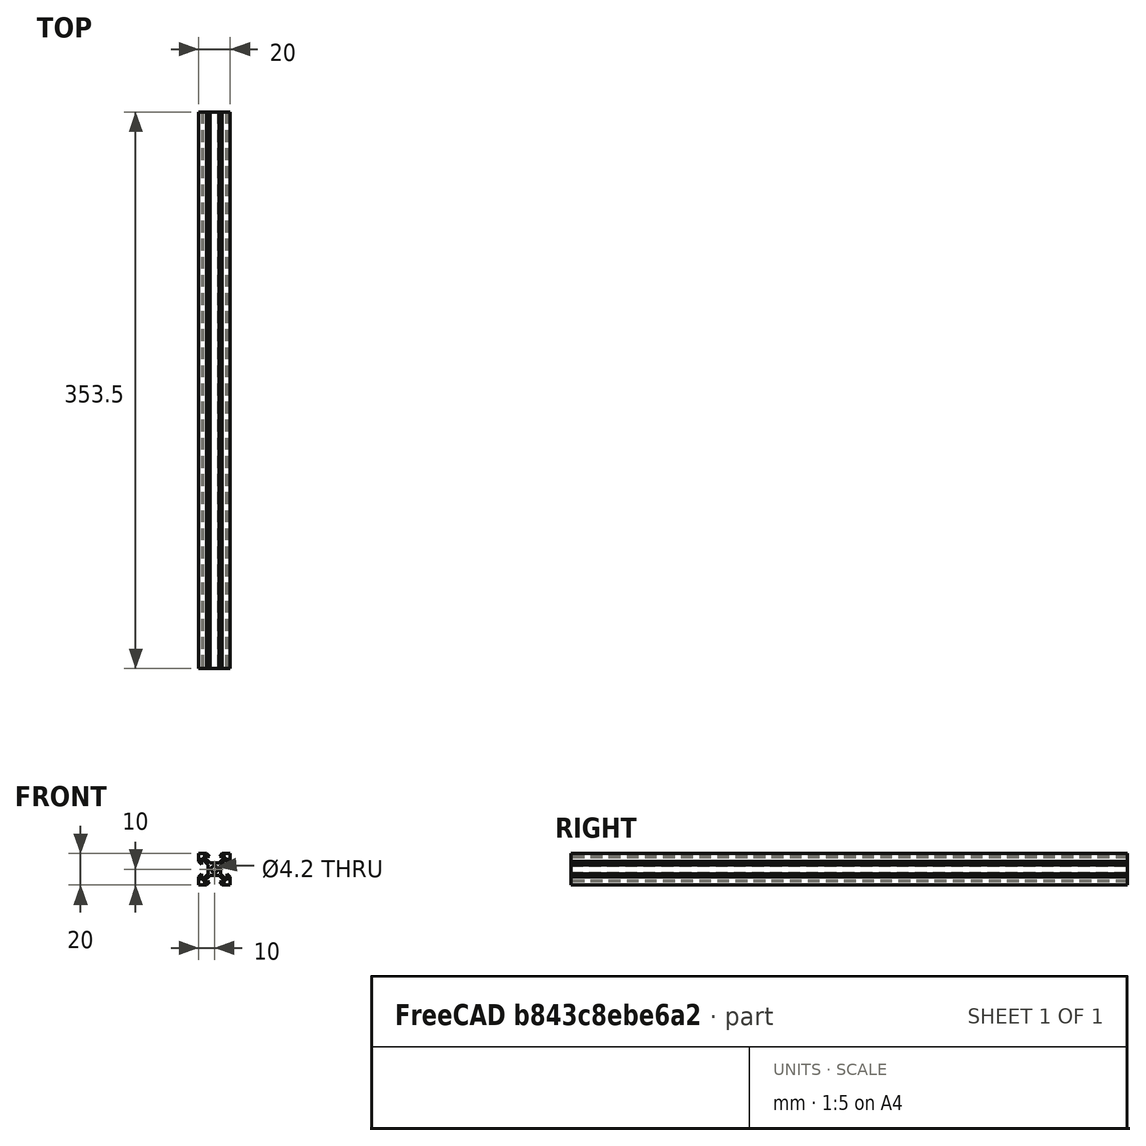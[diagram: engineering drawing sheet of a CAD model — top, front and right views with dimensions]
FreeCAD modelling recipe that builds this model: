
FCSTD DOCUMENT  (FreeCAD 0.20R29177 (Git))
Label: Vlot short Y
License: All rights reserved
LicenseURL: http://en.wikipedia.org/wiki/All_rights_reserved
objects: Sketcher::SketchObject×1, PartDesign::Pad×1, PartDesign::Body×1
note: 4 computed .brp shape members not serialized (recipe doc carries the construction recipe); baked Part::Feature solids carry a one-line shape summary decoded from their .brp

FEATURE [Sketcher::SketchObject] Sketch
  FullyConstrained = true
  MapMode = 5
  Placement = pos=(0,0,0) rot=(1,0,0;1.5708rad)
  Support = -> [XZ_Plane]
  sketch-geometry (43):
    g0: LineSegment StartX=0 StartY=0 StartZ=0 EndX=5.05 EndY=0 EndZ=0
    g1: LineSegment StartX=20 StartY=20 StartZ=0 EndX=14.95 EndY=20 EndZ=0
    g2: LineSegment StartX=0 StartY=20 StartZ=0 EndX=0 EndY=14.95 EndZ=0
    g3: LineSegment StartX=5.05 StartY=20 StartZ=0 EndX=6.9 EndY=18.15 EndZ=0
    g4: LineSegment StartX=6.9 StartY=18.15 StartZ=0 EndX=2.91066 EndY=18.15 EndZ=0
    g5: LineSegment StartX=2.91066 StartY=18.15 StartZ=0 EndX=7.16066 EndY=13.9 EndZ=0
    g6: LineSegment StartX=7.16066 StartY=13.9 StartZ=0 EndX=12.8393 EndY=13.9 EndZ=0
    g7: LineSegment StartX=12.8393 StartY=13.9 StartZ=0 EndX=17.0893 EndY=18.15 EndZ=0
    g8: LineSegment StartX=17.0893 StartY=18.15 StartZ=0 EndX=13.1 EndY=18.15 EndZ=0
    g9: LineSegment StartX=13.1 StartY=18.15 StartZ=0 EndX=14.95 EndY=20 EndZ=0
    g10: LineSegment StartX=0 StartY=20 StartZ=0 EndX=2.91066 EndY=18.15 EndZ=0
    g11: LineSegment StartX=17.0893 StartY=18.15 StartZ=0 EndX=20 EndY=20 EndZ=0
    g12: LineSegment StartX=0 StartY=20 StartZ=0 EndX=20 EndY=0 EndZ=0
    g13: LineSegment StartX=5.05 StartY=20 StartZ=0 EndX=0 EndY=20 EndZ=0
    g14: LineSegment StartX=0 StartY=20 StartZ=0 EndX=20 EndY=20 EndZ=0
    g15: LineSegment StartX=20 StartY=14.95 StartZ=0 EndX=18.15 EndY=13.1 EndZ=0
    g16: LineSegment StartX=18.15 StartY=13.1 StartZ=0 EndX=18.15 EndY=17.0893 EndZ=0
    g17: LineSegment StartX=18.15 StartY=17.0893 StartZ=0 EndX=13.9 EndY=12.8393 EndZ=0
    g18: LineSegment StartX=13.9 StartY=12.8393 StartZ=0 EndX=13.9 EndY=7.16066 EndZ=0
    g19: LineSegment StartX=13.9 StartY=7.16066 StartZ=0 EndX=18.15 EndY=2.91066 EndZ=0
    g20: LineSegment StartX=20 StartY=14.95 StartZ=0 EndX=20 EndY=20 EndZ=0
    g21: LineSegment StartX=18.15 StartY=2.91066 StartZ=0 EndX=18.15 EndY=6.9 EndZ=0
    g22: LineSegment StartX=18.15 StartY=6.9 StartZ=0 EndX=20 EndY=5.05 EndZ=0
    g23: LineSegment StartX=20 StartY=5.05 StartZ=0 EndX=20 EndY=0 EndZ=0
    g24: LineSegment StartX=5.05 StartY=0 StartZ=0 EndX=6.9 EndY=1.85 EndZ=0
    g25: LineSegment StartX=6.9 StartY=1.85 StartZ=0 EndX=2.91066 EndY=1.85 EndZ=0
    g26: LineSegment StartX=2.91066 StartY=1.85 StartZ=0 EndX=7.16066 EndY=6.1 EndZ=0
    g27: LineSegment StartX=7.16066 StartY=6.1 StartZ=0 EndX=12.8393 EndY=6.1 EndZ=0
    g28: LineSegment StartX=12.8393 StartY=6.1 StartZ=0 EndX=17.0893 EndY=1.85 EndZ=0
    g29: LineSegment StartX=17.0893 StartY=1.85 StartZ=0 EndX=13.1 EndY=1.85 EndZ=0
    g30: LineSegment StartX=13.1 StartY=1.85 StartZ=0 EndX=14.95 EndY=0 EndZ=0
    g31: LineSegment StartX=14.95 StartY=0 StartZ=0 EndX=20 EndY=0 EndZ=0
    g32: LineSegment StartX=0 StartY=14.95 StartZ=0 EndX=1.85 EndY=13.1 EndZ=0
    g33: LineSegment StartX=1.85 StartY=13.1 StartZ=0 EndX=1.85 EndY=17.0893 EndZ=0
    g34: LineSegment StartX=1.85 StartY=17.0893 StartZ=0 EndX=6.1 EndY=12.8393 EndZ=0
    g35: LineSegment StartX=6.1 StartY=12.8393 StartZ=0 EndX=6.1 EndY=7.16066 EndZ=0
    g36: LineSegment StartX=6.1 StartY=7.16066 StartZ=0 EndX=1.85 EndY=2.91066 EndZ=0
    g37: LineSegment StartX=1.85 StartY=2.91066 StartZ=0 EndX=1.85 EndY=6.9 EndZ=0
    g38: LineSegment StartX=1.85 StartY=6.9 StartZ=0 EndX=-2e-16 EndY=5.05 EndZ=0
    g39: LineSegment StartX=-2e-16 StartY=5.05 StartZ=0 EndX=0 EndY=0 EndZ=0
    g40: LineSegment StartX=0 StartY=20 StartZ=0 EndX=0 EndY=0 EndZ=0
    g41: LineSegment StartX=0 StartY=0 StartZ=0 EndX=10 EndY=10 EndZ=0
    g42: Circle CenterX=10 CenterY=10 CenterZ=0 NormalX=0 NormalY=0 NormalZ=1 AngleXU=0 Radius=2.1
  constraints (119):
    c: Coincident(g20,g1)
    c: Coincident(g13,g2)
    c: Coincident(g39,g0)
    c: Horizontal(g0)
    c: Horizontal(g1)
    c: Vertical(g2)
    c: Coincident(g0,g-1)
    c: DistanceY(g39,g2) = 20
    c: Coincident(g4,g3)
    c: Horizontal(g4)
    c: Coincident(g6,g5)
    c: Horizontal(g6)
    c: Coincident(g8,g7)
    c: Horizontal(g8)
    c: Coincident(g9,g8)
    c: Equal(g3,g9)
    c: Equal(g8,g4)
    c: Equal(g5,g7)
    c: Coincident(g4,g5)
    c: PointOnObject(g3,g8)
    c: Coincident(g7,g6)
    c: Coincident(g10,g13)
    c: Coincident(g10,g4)
    c: Coincident(g11,g7)
    c: Coincident(g11,g20)
    c: Equal(g10,g11)
    c: Coincident(g12,g13)
    c: Coincident(g12,g31)
    c: Parallel(g5,g12)
    c: Parallel(g3,g5)
    c: DistanceY(g3,g3) = 1.85
    c: DistanceY(g5,g3) = 6.1
    c: DistanceX(g3,g8) = 6.2
    c: Distance(g5,g12) = 0.75
    c: Coincident(g1,g9)
    c: Coincident(g13,g3)
    c: Tangent(g1,g13)
    c: Coincident(g14,g2)
    c: Coincident(g14,g20)
    c: Coincident(g16,g15)
    c: Coincident(g17,g16)
    c: Coincident(g18,g17)
    c: Vertical(g18)
    c: Coincident(g19,g18)
    c: Coincident(g20,g15)
    c: Equal(g9,g15)
    c: Vertical(g16)
    c: Equal(g17,g19)
    c: Parallel(g7,g17)
    c: Parallel(g17,g15)
    c: Parallel(g19,g12)
    c: Equal(g17,g7)
    c: Equal(g18,g6)
    c: Vertical(g20)
    c: Equal(g16,g8)
    c: Equal(g1,g20)
    c: Coincident(g21,g19)
    c: Vertical(g21)
    c: Coincident(g22,g21)
    c: Coincident(g23,g22)
    c: Coincident(g23,g31)
    c: Equal(g16,g21)
    c: Equal(g22,g15)
    c: Equal(g23,g20)
    c: Coincident(g25,g24)
    c: Horizontal(g25)
    c: Coincident(g26,g25)
    c: Horizontal(g27)
    c: Coincident(g29,g28)
    c: Horizontal(g29)
    c: Coincident(g30,g29)
    c: Equal(g24,g30)
    c: Equal(g29,g25)
    c: Equal(g26,g28)
    c: Coincident(g28,g27)
    c: Coincident(g27,g26)
    c: Parallel(g28,g12)
    c: Parallel(g24,g26)
    c: Parallel(g26,g17)
    c: Equal(g30,g22)
    c: Equal(g28,g19)
    c: Equal(g27,g18)
    c: Equal(g29,g21)
    c: Coincident(g0,g24)
    c: Coincident(g31,g30)
    c: Tangent(g0,g31)
    c: Vertical(g23)
    c: Equal(g23,g31)
    c: Coincident(g33,g32)
    c: Vertical(g33)
    c: Coincident(g34,g33)
    c: Coincident(g35,g34)
    c: Vertical(g35)
    c: Coincident(g36,g35)
    c: Coincident(g37,g36)
    c: Vertical(g37)
    c: Coincident(g38,g37)
    c: Coincident(g2,g32)
    c: Coincident(g39,g38)
    c: Tangent(g2,g39)
    c: Equal(g32,g38)
    c: Equal(g36,g34)
    c: Equal(g35,g27)
    c: Equal(g26,g36)
    c: Equal(g38,g24)
    c: Equal(g0,g39)
    c: Parallel(g38,g36)
    c: Parallel(g38,g26)
    c: Parallel(g34,g32)
    c: Equal(g2,g13)
    c: Equal(g33,g4)
    c: Coincident(g40,g2)
    c: Coincident(g40,g0)
    c: Equal(g14,g40)
    c: Coincident(g41,g0)
    c: PointOnObject(g41,g12)
    c: Perpendicular(g12,g41)
    c: Coincident(g42,g41)
    c: Diameter(g42) = 4.2
FEATURE [PartDesign::Pad] Pad
  Direction = (1,1,1)
  Length = 353.5
  Length2 = 100
  Placement = pos=(0,0,0) rot=(1,0,0;1.5708rad)
  Profile = -> Sketch
  Type = 0
FEATURE [PartDesign::Body] Body  label="Vslot 1"
  Group = -> [Sketch,Pad]
  Origin = -> Origin
  Tip = -> Pad
